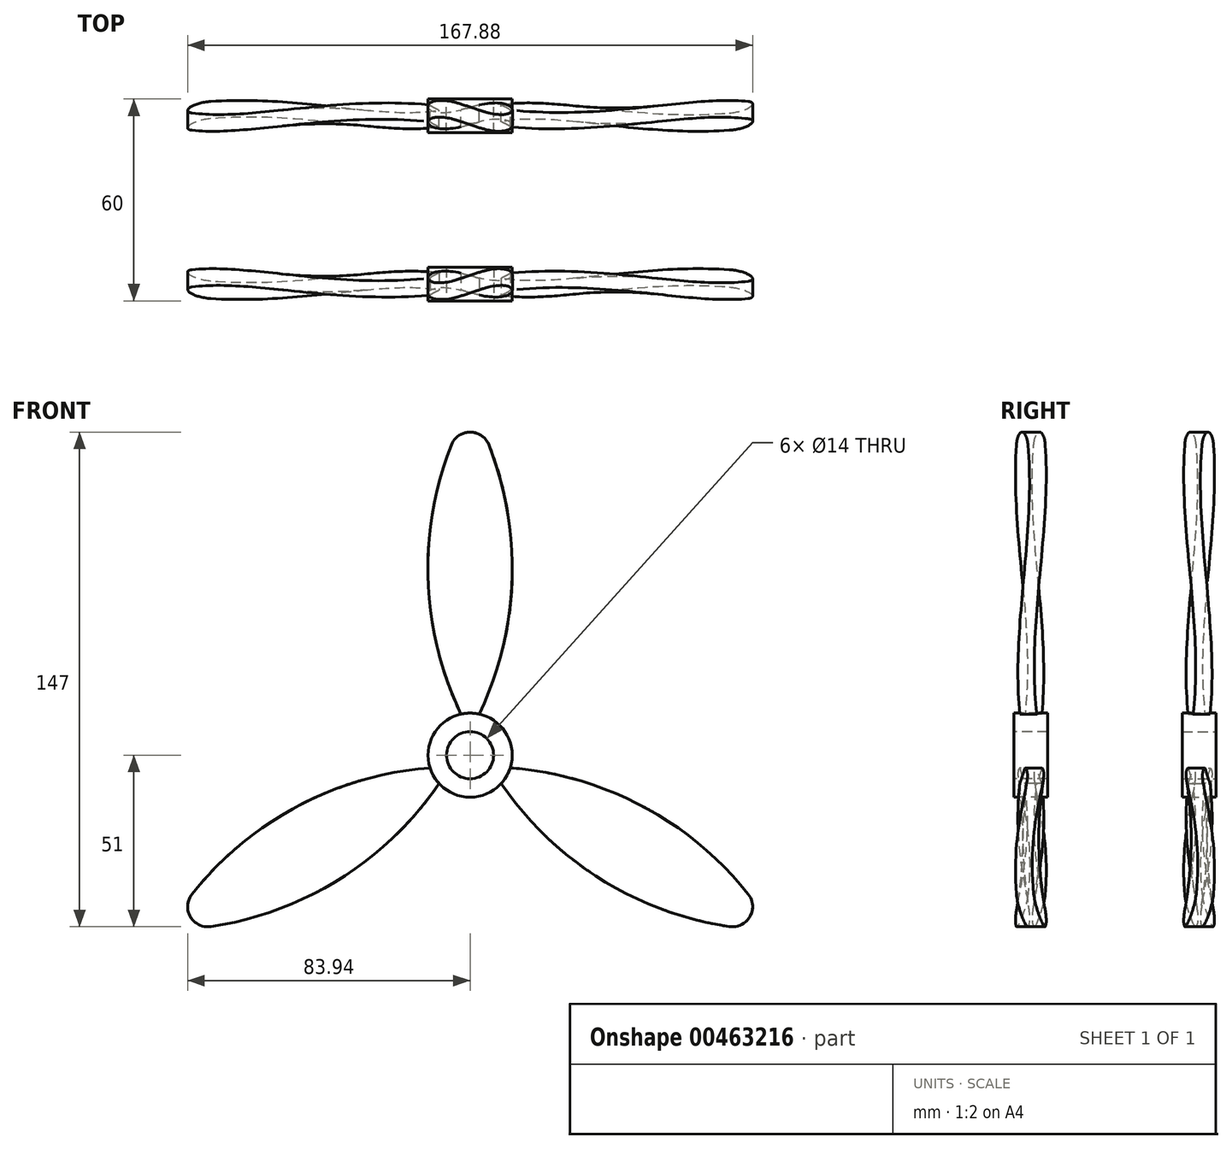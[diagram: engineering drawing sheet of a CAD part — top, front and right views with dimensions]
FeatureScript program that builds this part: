
annotation { "Feature Type Name" : "Feature", "Feature Type Description" : "" }
export const myFeature = defineFeature(function(context is Context, id is Id, definition is map)
    precondition{}
    {
        {
            var Q0;
            Q0=qCreatedBy(makeId("Top.planeOp"),FACE);
            var sketch = newSketch(context, id + "F0", { "sketchPlane" : qUnion([Q0])});
            skLineSegment(sketch, "E0", {"start": v(0, 55.99) * mm, "end": v(0, -40.51) * mm, "construction": true});
            skLineSegment(sketch, "E1", {"start": v(-50.98, 0) * mm, "end": v(55.53, 0) * mm, "construction": true});
            skLineSegment(sketch, "E2", {"start": v(-24.35, -6.2) * mm, "end": v(-22.64, -10.9) * mm});
            skLineSegment(sketch, "E3", {"start": v(-22.64, -10.9) * mm, "end": v(24.35, 6.2) * mm});
            skLineSegment(sketch, "E4", {"start": v(24.35, 6.2) * mm, "end": v(22.64, 10.9) * mm});
            skLineSegment(sketch, "E5", {"start": v(22.64, 10.9) * mm, "end": v(-24.35, -6.2) * mm});
            skLineSegment(sketch, "E6", {"start": v(-0.86, 2.35) * mm, "end": v(0.86, -2.35) * mm, "construction": true});
            skLineSegment(sketch, "E7", {"start": v(-23.5, -8.55) * mm, "end": v(23.5, 8.55) * mm, "construction": true});
            skSolve(sketch);
        }
        {
            var Q0;
            Q0=qCreatedBy(makeId("Top.planeOp"),FACE);
            cPlane(context, id + "F1", {"entities" : qUnion([Q0]), "cplaneType" : CPlaneType.OFFSET, "offset" : 100 * mm, "width" : 150 * mm, "height" : 150 * mm});
        }
        {
            var Q0;
            Q0=qCreatedBy(id+"F1.planeOp",FACE);
            var sketch = newSketch(context, id + "F2", { "sketchPlane" : qUnion([Q0])});
            skLineSegment(sketch, "E8", {"start": v(0, 41.88) * mm, "end": v(0, -37.33) * mm, "construction": true});
            skLineSegment(sketch, "E9", {"start": v(-42.79, 0) * mm, "end": v(50.53, 0) * mm, "construction": true});
            skLineSegment(sketch, "E10", {"start": v(-22.64, 10.9) * mm, "end": v(-24.35, 6.2) * mm});
            skLineSegment(sketch, "E11", {"start": v(-24.35, 6.2) * mm, "end": v(22.64, -10.9) * mm});
            skLineSegment(sketch, "E12", {"start": v(22.64, -10.9) * mm, "end": v(24.35, -6.2) * mm});
            skLineSegment(sketch, "E13", {"start": v(24.35, -6.2) * mm, "end": v(-22.64, 10.9) * mm});
            skLineSegment(sketch, "E14", {"start": v(-23.5, 8.55) * mm, "end": v(23.5, -8.55) * mm, "construction": true});
            skLineSegment(sketch, "E15", {"start": v(0.86, 2.35) * mm, "end": v(-0.86, -2.35) * mm, "construction": true});
            skSolve(sketch);
        }
        {
            var Q0;
            Q0=makeQuery(id+"F2.imprint","IMPRINT",FACE,{"disambiguationData":[TD([[makeQuery(id+"F2.imprint","IMPRINT",EDGE,{"derivedFrom":sQuery(id+"F2.wireOp",EDGE,"E10")}),1.0]])]});
            var Q1;
            Q1=makeQuery(id+"F0.imprint","IMPRINT",FACE,{"disambiguationData":[TD([[makeQuery(id+"F0.imprint","IMPRINT",EDGE,{"derivedFrom":sQuery(id+"F0.wireOp",EDGE,"E2")}),1.0]])]});
            loft(context, id + "F3", {"sheetProfilesArray" : [{ "sheetProfileEntities" : qUnion([Q0]) }, { "sheetProfileEntities" : qUnion([Q1]) }]});
        }
        {
            var Q0;
            Q0=qCreatedBy(makeId("Front.planeOp"),FACE);
            var sketch = newSketch(context, id + "F4", { "sketchPlane" : qUnion([Q0])});
            skLineSegment(sketch, "E16", {"start": v(0, 234.2) * mm, "end": v(0, -21.65) * mm, "construction": true});
            skArc(sketch, "E17", {"start": v(0, 7) * mm, "mid": v(12.34, 48.98) * mm, "end": v(5.58, 92.2) * mm});
            skArc(sketch, "E18", {"start": v(5.58, 92.2) * mm, "mid": v(3.38, 94.96) * mm, "end": v(0, 96) * mm});
            skArc(sketch, "E19.MirrorCS", {"start": v(-5.58, 92.2) * mm, "mid": v(-3.38, 94.96) * mm, "end": v(0, 96) * mm});
            skArc(sketch, "E20.MirrorCS", {"start": v(0, 7) * mm, "mid": v(-12.34, 48.98) * mm, "end": v(-5.58, 92.2) * mm});
            skSolve(sketch);
        }
        {
            var Q0;
            Q0 = qSketchRegion(id + "F4", true);
            extrude(context, id + "F5", {"entities" : qUnion([Q0]), "operationType" : NewBodyOperationType.INTERSECT, "endBound" : BoundingType.SYMMETRIC, "depth" : 20 * mm});
        }
        {
            var Q0;
            Q0=qCreatedBy(makeId("Front.planeOp"),FACE);
            var sketch = newSketch(context, id + "F6", { "sketchPlane" : qUnion([Q0])});
            skCircle(sketch, "E21", {"center": v(0, 0) * mm, "radius": 12.5 * mm});
            skCircle(sketch, "E22", {"center": v(0, 0) * mm, "radius": 7 * mm});
            skSolve(sketch);
        }
        {
            var Q0;
            Q0=makeQuery(id+"F6.imprint","IMPRINT",FACE,{"disambiguationData":[TD([[makeQuery(id+"F6.imprint","IMPRINT",EDGE,{"derivedFrom":sQuery(id+"F6.wireOp",EDGE,"E21")}),1.0]])]});
            extrude(context, id + "F7", {"entities" : qUnion([Q0]), "operationType" : NewBodyOperationType.ADD, "endBound" : BoundingType.SYMMETRIC, "depth" : 10 * mm});
        }
        {
            var Q0;
            Q0=makeQuery(id+"F3.opLoft","SWEPT_BODY",BODY,{"disambiguationData":[OSD([makeQuery(id+"F0.imprint","IMPRINT",FACE,{"disambiguationData":[TD([[makeQuery(id+"F0.imprint","IMPRINT",EDGE,{"derivedFrom":sQuery(id+"F0.wireOp",EDGE,"E2")}),1.0]])]}),makeQuery(id+"F2.imprint","IMPRINT",FACE,{"disambiguationData":[TD([[makeQuery(id+"F2.imprint","IMPRINT",EDGE,{"derivedFrom":sQuery(id+"F2.wireOp",EDGE,"E10")}),1.0]])]})])]});
            var Q1;
            Q1=makeQuery(id+"F7.opExtrude","SWEPT_FACE",FACE,{"disambiguationData":[OSD([sQuery(id+"F6.wireOp",EDGE,"E21")])]});
            circularPattern(context, id + "F8", {"entities" : qUnion([Q0]), "axis" : qUnion([Q1]), "angle" : 360 * degree, "instanceCount" : 3, "equalSpace" : true});
        }
        {
            var Q0;
            Q0=qCreatedBy(makeId("Front.planeOp"),FACE);
            cPlane(context, id + "F9", {"entities" : qUnion([Q0]), "cplaneType" : CPlaneType.OFFSET, "offset" : 25 * mm, "width" : 150 * mm, "height" : 150 * mm});
        }
        {
            var Q0;
            Q0=makeQuery(id+"F3.opLoft","SWEPT_BODY",BODY,{"disambiguationData":[OSD([makeQuery(id+"F0.imprint","IMPRINT",FACE,{"disambiguationData":[TD([[makeQuery(id+"F0.imprint","IMPRINT",EDGE,{"derivedFrom":sQuery(id+"F0.wireOp",EDGE,"E2")}),1.0]])]}),makeQuery(id+"F2.imprint","IMPRINT",FACE,{"disambiguationData":[TD([[makeQuery(id+"F2.imprint","IMPRINT",EDGE,{"derivedFrom":sQuery(id+"F2.wireOp",EDGE,"E10")}),1.0]])]})])]});
            var Q1;
            Q1=makeQuery(id+"F8.opPattern","COPY",BODY,{"derivedFrom":makeQuery(id+"F3.opLoft","SWEPT_BODY",BODY,{"disambiguationData":[OSD([makeQuery(id+"F0.imprint","IMPRINT",FACE,{"disambiguationData":[TD([[makeQuery(id+"F0.imprint","IMPRINT",EDGE,{"derivedFrom":sQuery(id+"F0.wireOp",EDGE,"E2")}),1.0]])]}),makeQuery(id+"F2.imprint","IMPRINT",FACE,{"disambiguationData":[TD([[makeQuery(id+"F2.imprint","IMPRINT",EDGE,{"derivedFrom":sQuery(id+"F2.wireOp",EDGE,"E10")}),1.0]])]})])]}),"instanceName":"1"});
            var Q2;
            Q2=makeQuery(id+"F8.opPattern","COPY",BODY,{"derivedFrom":makeQuery(id+"F3.opLoft","SWEPT_BODY",BODY,{"disambiguationData":[OSD([makeQuery(id+"F0.imprint","IMPRINT",FACE,{"disambiguationData":[TD([[makeQuery(id+"F0.imprint","IMPRINT",EDGE,{"derivedFrom":sQuery(id+"F0.wireOp",EDGE,"E2")}),1.0]])]}),makeQuery(id+"F2.imprint","IMPRINT",FACE,{"disambiguationData":[TD([[makeQuery(id+"F2.imprint","IMPRINT",EDGE,{"derivedFrom":sQuery(id+"F2.wireOp",EDGE,"E10")}),1.0]])]})])]}),"instanceName":"2"});
            var Q3;
            Q3=qCreatedBy(id+"F9.planeOp",FACE);
            mirror(context, id + "F10", {"entities" : qUnion([Q0, Q1, Q2]), "mirrorPlane" : qUnion([Q3])});
        }
    });
